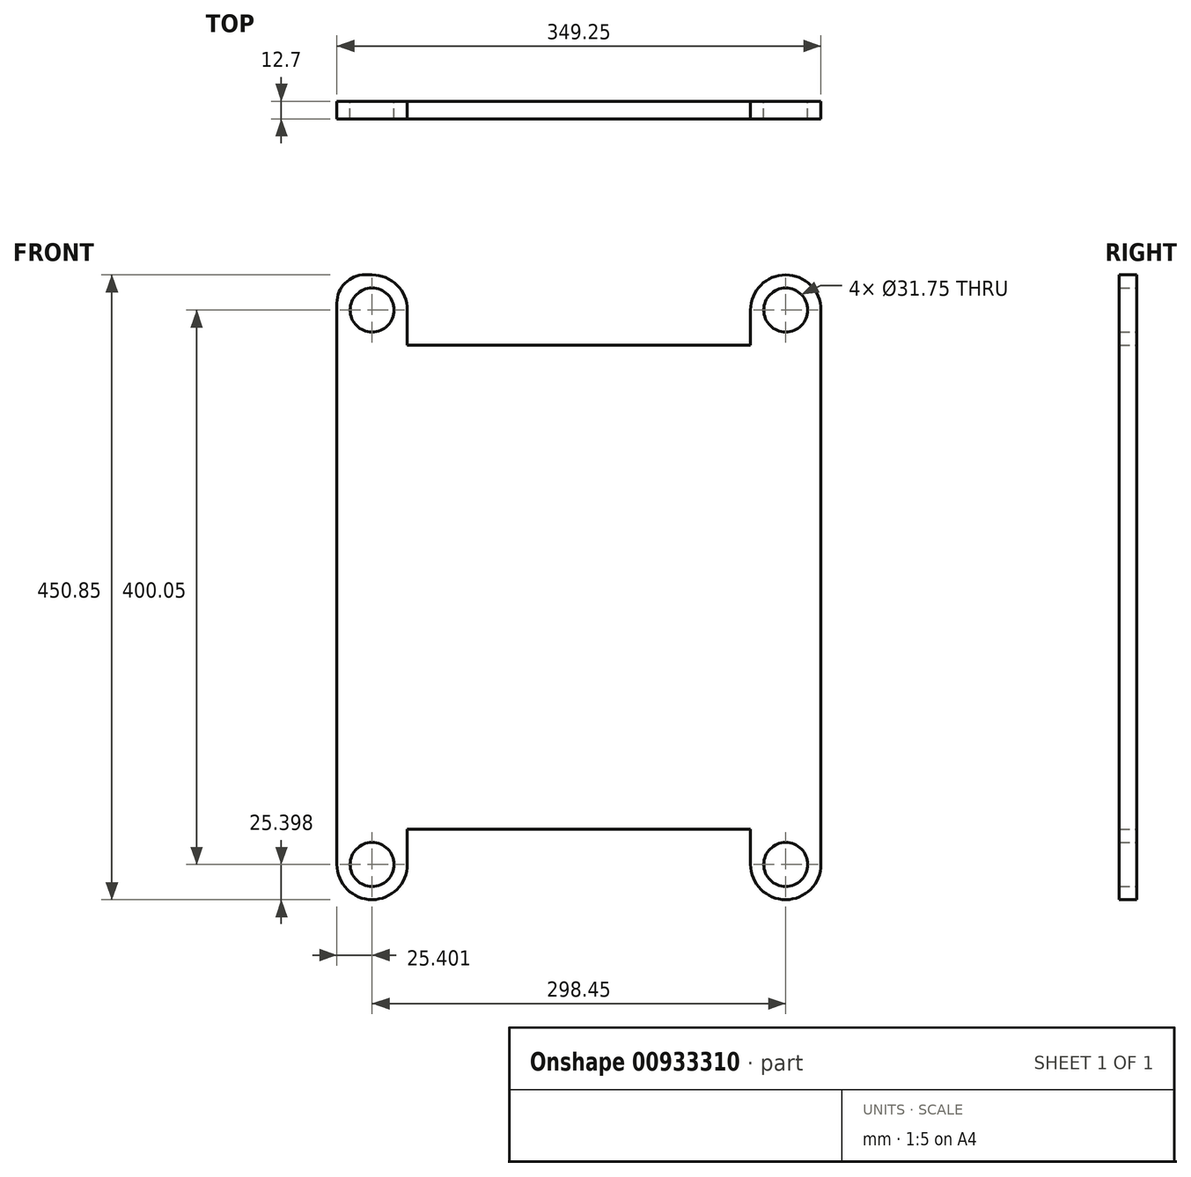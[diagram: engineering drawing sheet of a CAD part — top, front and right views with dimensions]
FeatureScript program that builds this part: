
annotation { "Feature Type Name" : "Feature", "Feature Type Description" : "" }
export const myFeature = defineFeature(function(context is Context, id is Id, definition is map)
    precondition{}
    {
        {
            var Q0;
            Q0=qCreatedBy(makeId("Front.planeOp"),FACE);
            var sketch = newSketch(context, id + "F0", { "sketchPlane" : qUnion([Q0])});
            skLineSegment(sketch, "E0.bottom", {"start": v(1.6, 451) * mm, "end": v(6.68, 451) * mm});
            skLineSegment(sketch, "E0.top", {"start": v(6.68, 0.16) * mm, "end": v(6.68, 0.16) * mm});
            skLineSegment(sketch, "E0.left", {"start": v(-18.72, 430.69) * mm, "end": v(-18.72, 25.56) * mm});
            skLineSegment(sketch, "E0.right", {"start": v(330.53, 425.6) * mm, "end": v(330.53, 25.56) * mm});
            skCircle(sketch, "E1", {"center": v(6.68, 425.6) * mm, "radius": 15.88 * mm});
            skCircle(sketch, "E2", {"center": v(305.13, 425.6) * mm, "radius": 15.88 * mm});
            skLineSegment(sketch, "E3", {"start": v(-18.72, 225.58) * mm, "end": v(330.53, 225.58) * mm, "construction": true});
            skCircle(sketch, "E4.MirrorC", {"center": v(6.68, 25.56) * mm, "radius": 15.88 * mm});
            skCircle(sketch, "E5.MirrorC", {"center": v(305.13, 25.56) * mm, "radius": 15.88 * mm});
            skPoint(sketch, "E6.visualSharp", {"position": v(-18.72, 451) * mm});
            skArc(sketch, "E6.filletArc", {"start": v(1.6, 451) * mm, "mid": v(-12.77, 445.06) * mm, "end": v(-18.72, 430.69) * mm});
            skPoint(sketch, "E7.visualSharp", {"position": v(330.53, 451) * mm});
            skArc(sketch, "E7.filletArc", {"start": v(330.53, 425.6) * mm, "mid": v(323.1, 443.57) * mm, "end": v(305.13, 451) * mm});
            skPoint(sketch, "E8.visualSharp", {"position": v(-18.72, 0.16) * mm});
            skArc(sketch, "E8.filletArc", {"start": v(-18.72, 25.56) * mm, "mid": v(-11.28, 7.6) * mm, "end": v(6.68, 0.16) * mm});
            skPoint(sketch, "E9.visualSharp", {"position": v(330.53, 0.16) * mm});
            skArc(sketch, "E9.filletArc", {"start": v(305.13, 0.16) * mm, "mid": v(323.1, 7.6) * mm, "end": v(330.53, 25.56) * mm});
            skLineSegment(sketch, "E10", {"start": v(32.08, 25.56) * mm, "end": v(32.08, 50.96) * mm});
            skLineSegment(sketch, "E11", {"start": v(32.08, 50.96) * mm, "end": v(279.73, 50.96) * mm});
            skLineSegment(sketch, "E12", {"start": v(279.73, 50.96) * mm, "end": v(279.73, 25.56) * mm});
            skLineSegment(sketch, "E13.trimOffspring", {"start": v(305.13, 0.16) * mm, "end": v(305.13, 0.16) * mm});
            skPoint(sketch, "E14.visualSharp", {"position": v(32.08, 0.16) * mm});
            skArc(sketch, "E14.filletArc", {"start": v(6.68, 0.16) * mm, "mid": v(24.64, 7.6) * mm, "end": v(32.08, 25.56) * mm});
            skPoint(sketch, "E15.newPointB", {"position": v(279.73, 0) * mm});
            skArc(sketch, "E15.filletArc", {"start": v(279.73, 25.56) * mm, "mid": v(287.17, 7.6) * mm, "end": v(305.13, 0.16) * mm});
            skLineSegment(sketch, "E16.MirrorCS", {"start": v(32.08, 400.2) * mm, "end": v(279.73, 400.2) * mm});
            skLineSegment(sketch, "E17.MirrorCS", {"start": v(32.08, 425.6) * mm, "end": v(32.08, 400.2) * mm});
            skArc(sketch, "E18.MirrorCS", {"start": v(6.68, 451) * mm, "mid": v(24.64, 443.57) * mm, "end": v(32.08, 425.6) * mm});
            skLineSegment(sketch, "E19.MirrorCS", {"start": v(279.73, 400.2) * mm, "end": v(279.73, 425.6) * mm});
            skArc(sketch, "E20.MirrorCS", {"start": v(279.73, 425.6) * mm, "mid": v(287.17, 443.57) * mm, "end": v(305.13, 451) * mm});
            skSolve(sketch);
        }
        {
            var Q0;
            Q0 = qSketchRegion(id + "F0", true);
            extrude(context, id + "F1", {"entities" : qUnion([Q0]), "depth" : 12.7 * mm, "offsetDistance" : 25.4 * mm});
        }
    });
